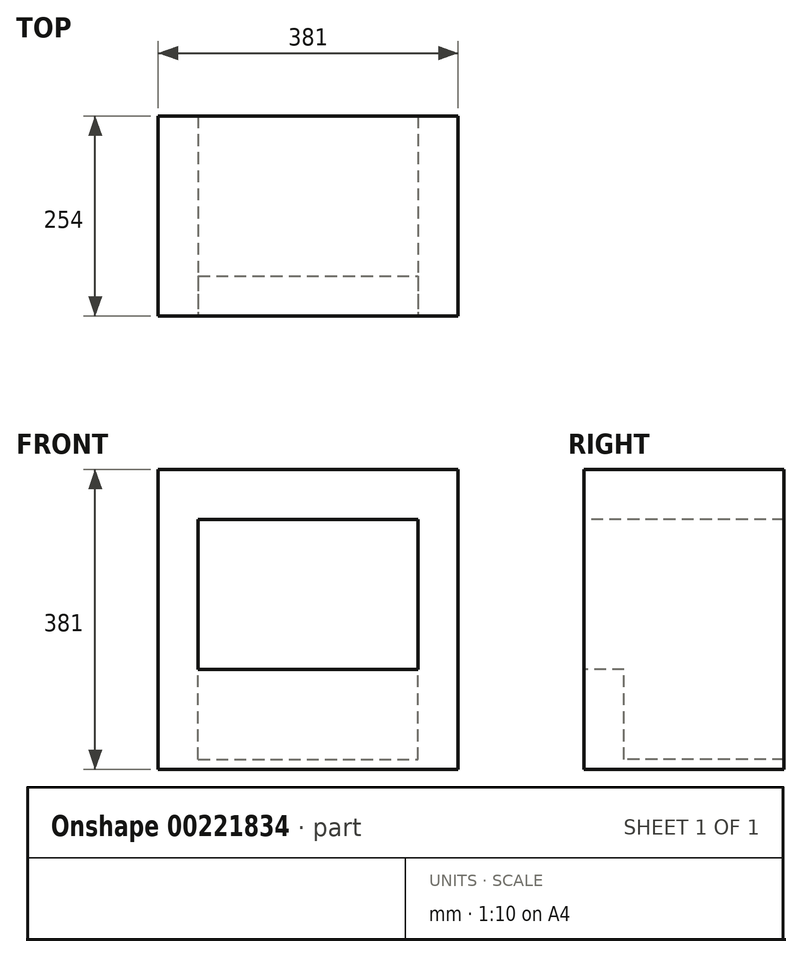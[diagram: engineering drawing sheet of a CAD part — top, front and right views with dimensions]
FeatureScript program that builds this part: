
annotation { "Feature Type Name" : "Feature", "Feature Type Description" : "" }
export const myFeature = defineFeature(function(context is Context, id is Id, definition is map)
    precondition{}
    {
        {
            var Q0;
            Q0=qCreatedBy(makeId("Top.planeOp"),FACE);
            var sketch = newSketch(context, id + "F0", { "sketchPlane" : qUnion([Q0])});
            skLineSegment(sketch, "E0.bottom", {"start": v(190.5, -127) * mm, "end": v(-190.5, -127) * mm});
            skLineSegment(sketch, "E0.top", {"start": v(190.5, 127) * mm, "end": v(-190.5, 127) * mm});
            skLineSegment(sketch, "E0.left", {"start": v(190.5, -127) * mm, "end": v(190.5, 127) * mm});
            skLineSegment(sketch, "E0.right", {"start": v(-190.5, -127) * mm, "end": v(-190.5, 127) * mm});
            skPoint(sketch, "E0.middle", {"position": v(0, 0) * mm});
            skSolve(sketch);
        }
        {
            var Q0;
            Q0 = qSketchRegion(id + "F0", true);
            extrude(context, id + "F1", {"entities" : qUnion([Q0]), "depth" : 381 * mm});
        }
        {
            var Q0;
            Q0=makeQuery(id+"F1.opExtrude","SWEPT_FACE",FACE,{"disambiguationData":[OSD([sQuery(id+"F0.wireOp",EDGE,"E0.bottom")])]});
            var sketch = newSketch(context, id + "F2", { "sketchPlane" : qUnion([Q0])});
            skLineSegment(sketch, "E1", {"start": v(0, 0) * mm, "end": v(0, 127) * mm, "construction": true});
            skPoint(sketch, "E1.endSnap0", {"position": v(0, 0) * mm});
            skLineSegment(sketch, "E2", {"start": v(0, 0) * mm, "end": v(0, 190.5) * mm, "construction": true});
            skLineSegment(sketch, "E3", {"start": v(-190.5, 190.5) * mm, "end": v(-139.7, 190.5) * mm, "construction": true});
            skLineSegment(sketch, "E4.bottom", {"start": v(-139.7, 127) * mm, "end": v(139.7, 127) * mm});
            skLineSegment(sketch, "E4.top", {"start": v(-139.7, 317.5) * mm, "end": v(139.7, 317.5) * mm});
            skLineSegment(sketch, "E4.left", {"start": v(-139.7, 127) * mm, "end": v(-139.7, 317.5) * mm});
            skLineSegment(sketch, "E4.right", {"start": v(139.7, 127) * mm, "end": v(139.7, 317.5) * mm});
            skSolve(sketch);
        }
        {
            var Q0;
            Q0 = qSketchRegion(id + "F2", true);
            extrude(context, id + "F3", {"entities" : qUnion([Q0]), "operationType" : NewBodyOperationType.REMOVE, "endBound" : BoundingType.THROUGH_ALL, "oppositeDirection" : true, "depth" : 25.4 * mm});
        }
        {
            var Q0;
            Q0=makeQuery(id+"F3.boolean.opBoolean","COPY",FACE,{"derivedFrom":makeQuery(id+"F3.opExtrude","SWEPT_FACE",FACE,{"disambiguationData":[OSD([sQuery(id+"F2.wireOp",EDGE,"E4.bottom")])]})});
            var sketch = newSketch(context, id + "F4", { "sketchPlane" : qUnion([Q0])});
            skLineSegment(sketch, "E5", {"start": v(0, 127) * mm, "end": v(0, -76.2) * mm, "construction": true});
            skLineSegment(sketch, "E6", {"start": v(0, -76.2) * mm, "end": v(-139.7, -76.2) * mm, "construction": true});
            skLineSegment(sketch, "E7.bottom", {"start": v(-139.7, -76.2) * mm, "end": v(139.7, -76.2) * mm});
            skLineSegment(sketch, "E7.top", {"start": v(-139.7, 127) * mm, "end": v(139.7, 127) * mm});
            skLineSegment(sketch, "E7.left", {"start": v(-139.7, -76.2) * mm, "end": v(-139.7, 127) * mm});
            skLineSegment(sketch, "E7.right", {"start": v(139.7, -76.2) * mm, "end": v(139.7, 127) * mm});
            skSolve(sketch);
        }
        {
            var Q0;
            Q0 = qSketchRegion(id + "F4", true);
            extrude(context, id + "F5", {"entities" : qUnion([Q0]), "operationType" : NewBodyOperationType.REMOVE, "oppositeDirection" : true, "depth" : 114.3 * mm});
        }
    });
